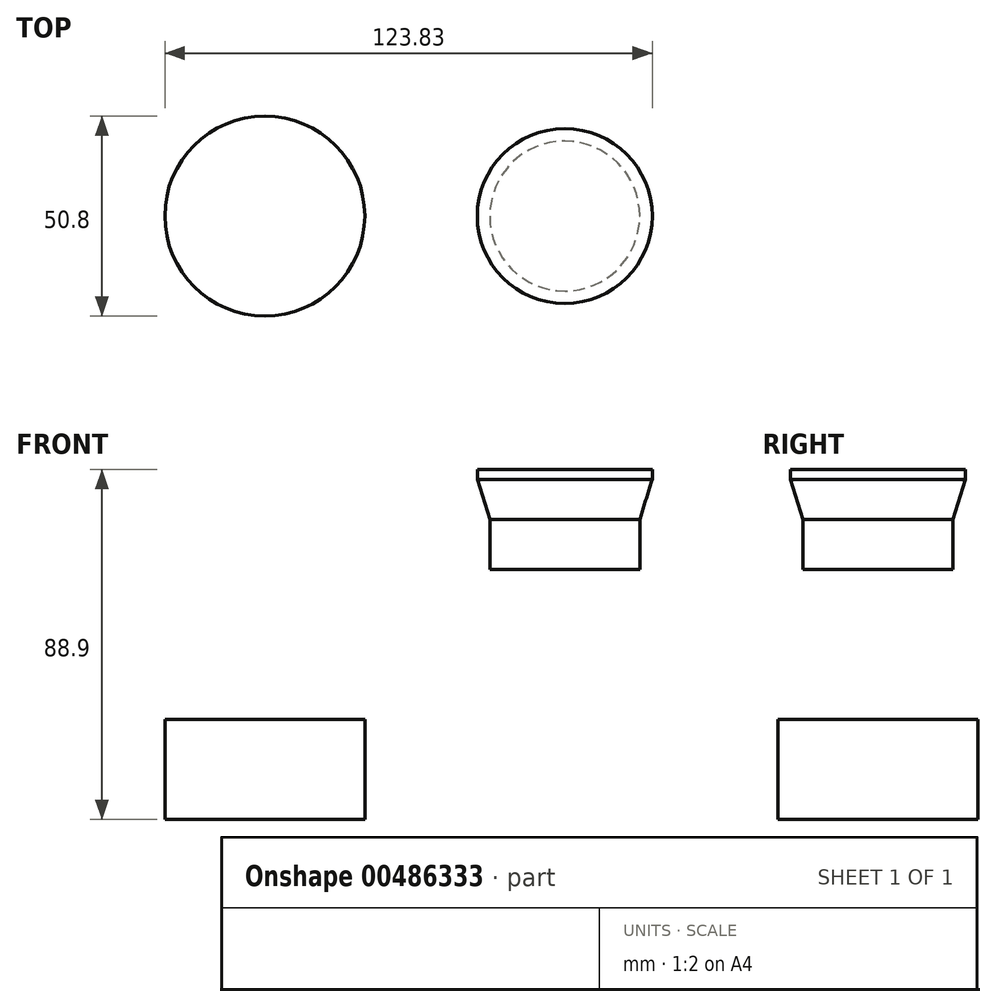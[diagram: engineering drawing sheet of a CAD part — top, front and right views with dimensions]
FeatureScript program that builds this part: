
annotation { "Feature Type Name" : "Feature", "Feature Type Description" : "" }
export const myFeature = defineFeature(function(context is Context, id is Id, definition is map)
    precondition{}
    {
        {
            var Q0;
            Q0=qCreatedBy(makeId("Top.planeOp"),FACE);
            var sketch = newSketch(context, id + "F0", { "sketchPlane" : qUnion([Q0])});
            skCircle(sketch, "E0", {"center": v(0, 0) * mm, "radius": 25.4 * mm});
            skSolve(sketch);
        }
        {
            var Q0;
            Q0 = qSketchRegion(id + "F0", true);
            extrude(context, id + "F1", {"entities" : qUnion([Q0]), "depth" : 25.4 * mm});
        }
        {
            var Q0;
            Q0=qCreatedBy(makeId("Top.planeOp"),FACE);
            cPlane(context, id + "F2", {"entities" : qUnion([Q0]), "cplaneType" : CPlaneType.OFFSET, "offset" : 76.2 * mm, "width" : 152.4 * mm, "height" : 152.4 * mm});
        }
        {
            var Q0;
            Q0=qCreatedBy(id+"F2.planeOp",FACE);
            var sketch = newSketch(context, id + "F3", { "sketchPlane" : qUnion([Q0])});
            skCircle(sketch, "E1", {"center": v(76.2, 0) * mm, "radius": 19.05 * mm});
            skSolve(sketch);
        }
        {
            var Q0;
            Q0 = qSketchRegion(id + "F3", true);
            extrude(context, id + "F4", {"entities" : qUnion([Q0]), "oppositeDirection" : true, "depth" : 12.7 * mm});
        }
        {
            var Q0;
            Q0=makeQuery(id+"F4.opExtrude","CAP_FACE",FACE,{"disambiguationData":[OSD([sQuery(id+"F3.wireOp",EDGE,"E1")])],"isStart":true});
            cPlane(context, id + "F5", {"entities" : qUnion([Q0]), "cplaneType" : CPlaneType.OFFSET, "offset" : 12.7 * mm, "width" : 152.4 * mm, "height" : 152.4 * mm});
        }
        {
            var Q0;
            Q0=qCreatedBy(id+"F5.planeOp",FACE);
            var sketch = newSketch(context, id + "F6", { "sketchPlane" : qUnion([Q0])});
            skCircle(sketch, "E2", {"center": v(76.2, 0) * mm, "radius": 22.22 * mm});
            skSolve(sketch);
        }
        {
            var Q0;
            Q0 = qSketchRegion(id + "F6", true);
            extrude(context, id + "F7", {"entities" : qUnion([Q0]), "oppositeDirection" : true, "depth" : 2.54 * mm});
        }
        {
            var Q0;
            Q0=makeQuery(id+"F4.opExtrude","CAP_FACE",FACE,{"disambiguationData":[OSD([sQuery(id+"F3.wireOp",EDGE,"E1")])],"isStart":true});
            var Q1;
            Q1=makeQuery(id+"F7.opExtrude","CAP_FACE",FACE,{"disambiguationData":[OSD([sQuery(id+"F6.wireOp",EDGE,"E2")])],"isStart":false});
            loft(context, id + "F8", {"sheetProfilesArray" : [{ "sheetProfileEntities" : qUnion([Q0]) }, { "sheetProfileEntities" : qUnion([Q1]) }]});
        }
    });
